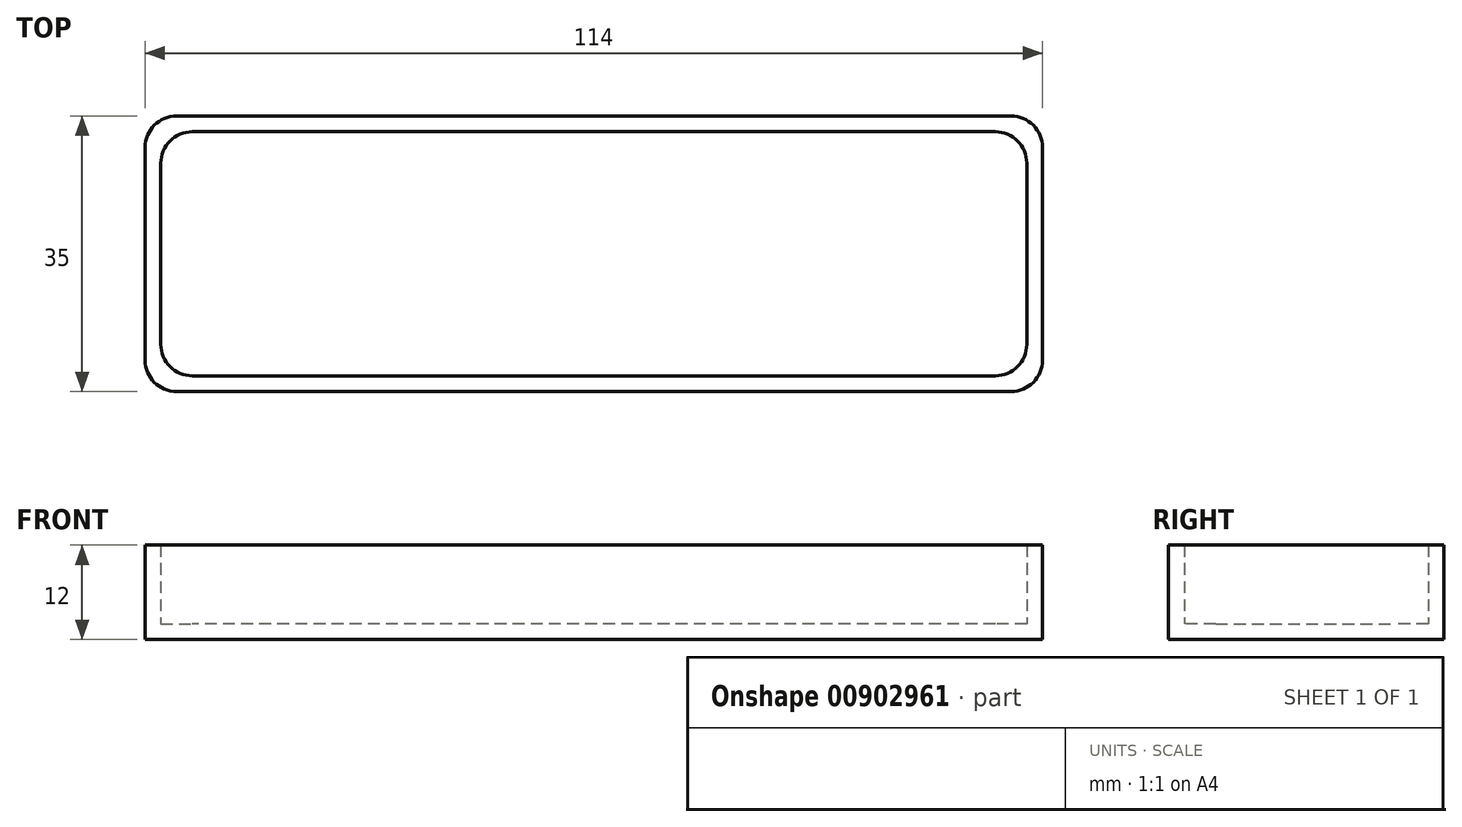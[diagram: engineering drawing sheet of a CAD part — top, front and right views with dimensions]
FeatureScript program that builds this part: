
annotation { "Feature Type Name" : "Feature", "Feature Type Description" : "" }
export const myFeature = defineFeature(function(context is Context, id is Id, definition is map)
    precondition{}
    {
        {
            var Q0;
            Q0=qCreatedBy(makeId("Top.planeOp"),FACE);
            var sketch = newSketch(context, id + "F0", { "sketchPlane" : qUnion([Q0])});
            skLineSegment(sketch, "E0.bottom", {"start": v(-53, 17.5) * mm, "end": v(53, 17.5) * mm});
            skLineSegment(sketch, "E0.top", {"start": v(-53, -17.5) * mm, "end": v(53, -17.5) * mm});
            skLineSegment(sketch, "E0.left", {"start": v(-57, 13.5) * mm, "end": v(-57, -13.5) * mm});
            skLineSegment(sketch, "E0.right", {"start": v(57, 13.5) * mm, "end": v(57, -13.5) * mm});
            skPoint(sketch, "E0.middle", {"position": v(0, 0) * mm});
            skLineSegment(sketch, "E1.0", {"start": v(-51, 15.5) * mm, "end": v(51, 15.5) * mm});
            skLineSegment(sketch, "E1.1", {"start": v(-55, 11.5) * mm, "end": v(-55, -11.5) * mm});
            skLineSegment(sketch, "E1.2", {"start": v(-51, -15.5) * mm, "end": v(51, -15.5) * mm});
            skLineSegment(sketch, "E1.3", {"start": v(55, 11.5) * mm, "end": v(55, -11.5) * mm});
            skPoint(sketch, "E2.visualSharp", {"position": v(-55, 15.5) * mm});
            skArc(sketch, "E2.filletArc", {"start": v(-51, 15.5) * mm, "mid": v(-53.83, 14.33) * mm, "end": v(-55, 11.5) * mm});
            skPoint(sketch, "E3.visualSharp", {"position": v(-55, -15.5) * mm});
            skArc(sketch, "E3.filletArc", {"start": v(-55, -11.5) * mm, "mid": v(-53.83, -14.33) * mm, "end": v(-51, -15.5) * mm});
            skPoint(sketch, "E4.visualSharp", {"position": v(55, -15.5) * mm});
            skArc(sketch, "E4.filletArc", {"start": v(51, -15.5) * mm, "mid": v(53.83, -14.33) * mm, "end": v(55, -11.5) * mm});
            skPoint(sketch, "E5.visualSharp", {"position": v(55, 15.5) * mm});
            skArc(sketch, "E5.filletArc", {"start": v(55, 11.5) * mm, "mid": v(53.83, 14.33) * mm, "end": v(51, 15.5) * mm});
            skPoint(sketch, "E6.visualSharp", {"position": v(-57, 17.5) * mm});
            skArc(sketch, "E6.filletArc", {"start": v(-53, 17.5) * mm, "mid": v(-55.83, 16.33) * mm, "end": v(-57, 13.5) * mm});
            skPoint(sketch, "E7.visualSharp", {"position": v(-57, -17.5) * mm});
            skArc(sketch, "E7.filletArc", {"start": v(-57, -13.5) * mm, "mid": v(-55.83, -16.33) * mm, "end": v(-53, -17.5) * mm});
            skPoint(sketch, "E8.visualSharp", {"position": v(57, -17.5) * mm});
            skArc(sketch, "E8.filletArc", {"start": v(53, -17.5) * mm, "mid": v(55.83, -16.33) * mm, "end": v(57, -13.5) * mm});
            skPoint(sketch, "E9.visualSharp", {"position": v(57, 17.5) * mm});
            skArc(sketch, "E9.filletArc", {"start": v(57, 13.5) * mm, "mid": v(55.83, 16.33) * mm, "end": v(53, 17.5) * mm});
            skSolve(sketch);
        }
        {
            var Q0;
            Q0=makeQuery(id+"F0.imprint","IMPRINT",FACE,{"disambiguationData":[TD([[makeQuery(id+"F0.imprint","IMPRINT",EDGE,{"derivedFrom":sQuery(id+"F0.wireOp",EDGE,"E1.0")}),-1.0]])]});
            var Q1;
            Q1=makeQuery(id+"F0.imprint","IMPRINT",FACE,{"disambiguationData":[TD([[makeQuery(id+"F0.imprint","IMPRINT",EDGE,{"derivedFrom":sQuery(id+"F0.wireOp",EDGE,"E0.bottom")}),-1.0]])]});
            extrude(context, id + "F1", {"entities" : qUnion([Q0, Q1]), "depth" : 2 * mm, "offsetDistance" : 25 * mm});
        }
        {
            var Q0;
            Q0=makeQuery(id+"F0.imprint","IMPRINT",FACE,{"disambiguationData":[TD([[makeQuery(id+"F0.imprint","IMPRINT",EDGE,{"derivedFrom":sQuery(id+"F0.wireOp",EDGE,"E0.bottom")}),-1.0]])]});
            extrude(context, id + "F2", {"entities" : qUnion([Q0]), "operationType" : NewBodyOperationType.ADD, "depth" : 12 * mm, "offsetDistance" : 25 * mm});
        }
    });
